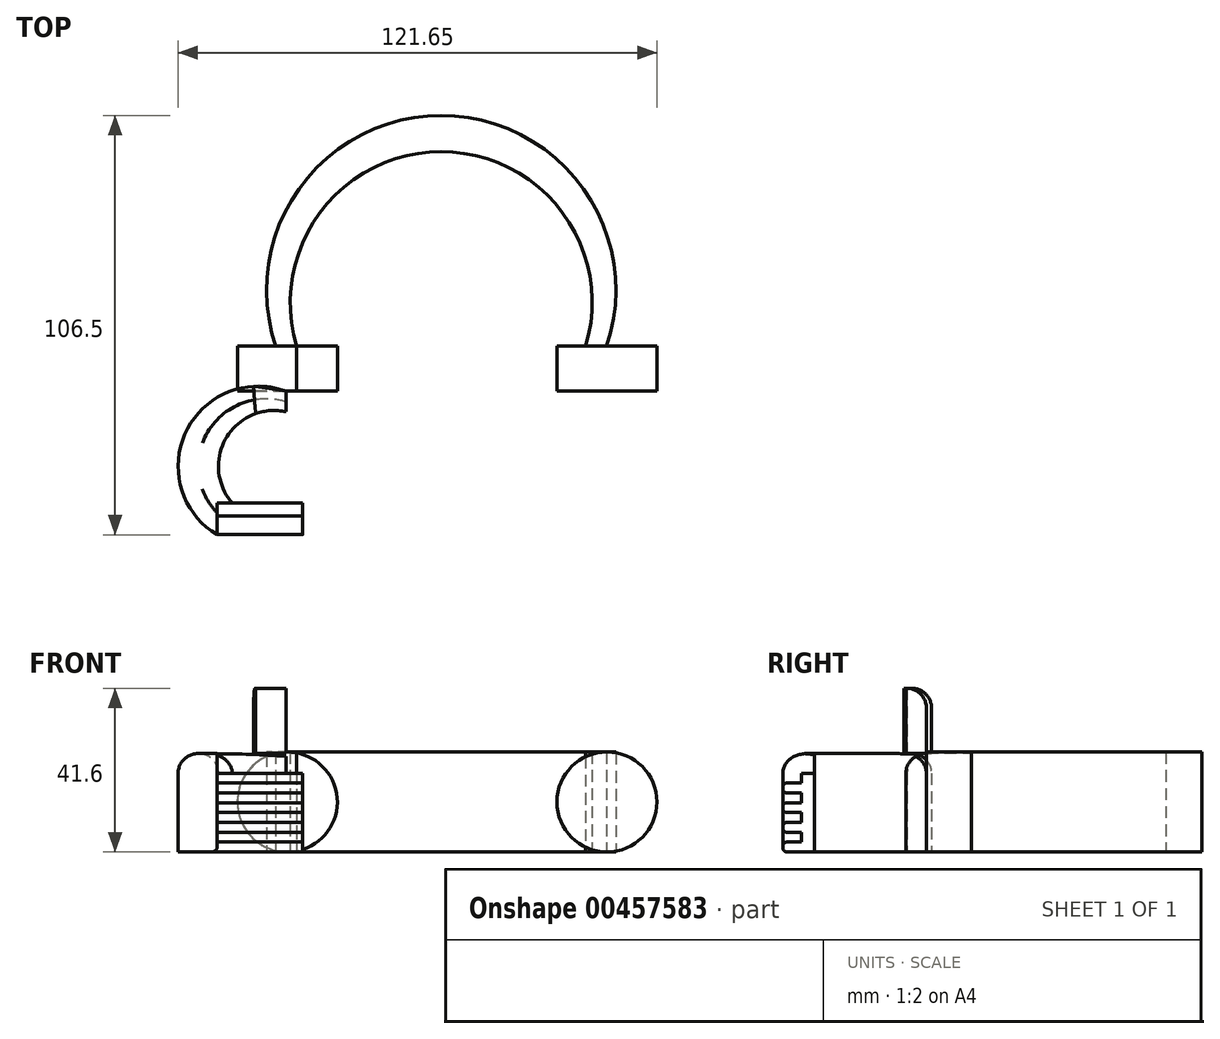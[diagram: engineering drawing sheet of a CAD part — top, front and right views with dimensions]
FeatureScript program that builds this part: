
annotation { "Feature Type Name" : "Feature", "Feature Type Description" : "" }
export const myFeature = defineFeature(function(context is Context, id is Id, definition is map)
    precondition{}
    {
        {
            var Q0;
            Q0=qCreatedBy(makeId("Top.planeOp"),FACE);
            var sketch = newSketch(context, id + "F0", { "sketchPlane" : qUnion([Q0])});
            skArc(sketch, "E0", {"start": v(46.23, 0) * mm, "mid": v(4.18, 58.57) * mm, "end": v(-37.87, 0) * mm});
            skLineSegment(sketch, "E1", {"start": v(-37.87, 0) * mm, "end": v(-32.54, 0) * mm});
            skLineSegment(sketch, "E2", {"start": v(46.23, 0) * mm, "end": v(40.9, 0) * mm});
            skArc(sketch, "E3", {"start": v(40.9, 0) * mm, "mid": v(4.18, 49.41) * mm, "end": v(-32.54, 0) * mm});
            skSolve(sketch);
        }
        {
            var Q0;
            Q0=makeQuery(id+"F0.imprint","IMPRINT",FACE,{"disambiguationData":[TD([[makeQuery(id+"F0.imprint","IMPRINT",EDGE,{"derivedFrom":sQuery(id+"F0.wireOp",EDGE,"E0")}),1.0]])]});
            extrude(context, id + "F1", {"entities" : qUnion([Q0]), "depth" : 25.4 * mm});
        }
        {
            var Q0;
            Q0=makeQuery(id+"F1.opExtrude","SWEPT_FACE",FACE,{"disambiguationData":[OSD([sQuery(id+"F0.wireOp",EDGE,"E1")])]});
            var sketch = newSketch(context, id + "F2", { "sketchPlane" : qUnion([Q0])});
            skCircle(sketch, "E4", {"center": v(-34.91, 12.7) * mm, "radius": 12.7 * mm});
            skCircle(sketch, "E5", {"center": v(46.29, 12.7) * mm, "radius": 12.7 * mm});
            skPoint(sketch, "E5.centerSnap0", {"position": v(-32.54, 12.7) * mm});
            skSolve(sketch);
        }
        {
            var Q0;
            {var subQ0=sQuery(id+"F2.wireOp",EDGE,"E4");var subQ1=makeQuery(id+"F1.opExtrude","SWEPT_EDGE",EDGE,{"disambiguationData":[OSD([sQuery(id+"F0.wireOp",EDGE,"E0"),sQuery(id+"F0.wireOp",EDGE,"E1")])]});var subQ2=makeQuery(id+"F2.imprint","INTERSECT",VERTEX,{"disambiguationData":[OD(0.0)],"derivedFrom":[subQ1,subQ0]});Q0=makeQuery(id+"F2.imprint","IMPRINT",FACE,{"disambiguationData":[TD([[makeQuery(id+"F2.imprint","IMPRINT",EDGE,{"disambiguationData":[TD([[subQ2,-1.0]])],"derivedFrom":subQ0}),1.0]])]});}
            var Q1;
            {var subQ0=sQuery(id+"F2.wireOp",EDGE,"E4");var subQ1=sQuery(id+"F0.wireOp",EDGE,"E1");var subQ5=makeQuery(id+"F2.imprint","INTERSECT",VERTEX,{"derivedFrom":[makeQuery(id+"F1.opExtrude","CAP_EDGE",EDGE,{"disambiguationData":[OSD([subQ1])],"isStart":true}),subQ0]});Q1=makeQuery(id+"F2.imprint","IMPRINT",FACE,{"disambiguationData":[TD([[makeQuery(id+"F2.imprint","IMPRINT",EDGE,{"disambiguationData":[TD([[subQ5,1.0]])],"derivedFrom":subQ0}),1.0]])]});}
            var Q2;
            {var subQ0=sQuery(id+"F2.wireOp",EDGE,"E4");var subQ1=makeQuery(id+"F1.opExtrude","SWEPT_EDGE",EDGE,{"disambiguationData":[OSD([sQuery(id+"F0.wireOp",EDGE,"E1"),sQuery(id+"F0.wireOp",EDGE,"E3")])]});var subQ2=makeQuery(id+"F2.imprint","INTERSECT",VERTEX,{"disambiguationData":[OD(0.0)],"derivedFrom":[subQ1,subQ0]});Q2=makeQuery(id+"F2.imprint","IMPRINT",FACE,{"disambiguationData":[TD([[makeQuery(id+"F2.imprint","IMPRINT",EDGE,{"disambiguationData":[TD([[subQ2,1.0]])],"derivedFrom":subQ0}),1.0]])]});}
            var Q3;
            Q3=sQuery(id+"F2.wireOp",EDGE,"E4");
            extrude(context, id + "F3", {"entities" : qUnion([Q0, Q1, Q2]), "surfaceEntities" : qUnion([Q3]), "depth" : 11.43 * mm});
        }
        {
            var Q0;
            Q0 = qSketchRegion(id + "F2", true);
            extrude(context, id + "F4", {"entities" : qUnion([Q0]), "depth" : 11.43 * mm});
        }
        {
            var Q0;
            Q0=qCreatedBy(makeId("Top.planeOp"),FACE);
            var sketch = newSketch(context, id + "F5", { "sketchPlane" : qUnion([Q0])});
            skArc(sketch, "E6", {"start": v(-35.28, -11.48) * mm, "mid": v(-62.66, -30.6) * mm, "end": v(-35.14, -49.5) * mm});
            skLineSegment(sketch, "E7", {"start": v(-35.14, -49.5) * mm, "end": v(-35.14, -44.34) * mm});
            skLineSegment(sketch, "E8", {"start": v(-35.28, -11.48) * mm, "end": v(-35.28, -16.68) * mm});
            skArc(sketch, "E9", {"start": v(-35.28, -16.68) * mm, "mid": v(-52.41, -30.6) * mm, "end": v(-35.14, -44.34) * mm});
            skSolve(sketch);
        }
        {
            var Q0;
            Q0=makeQuery(id+"F5.imprint","IMPRINT",FACE,{"disambiguationData":[TD([[makeQuery(id+"F5.imprint","IMPRINT",EDGE,{"derivedFrom":sQuery(id+"F5.wireOp",EDGE,"E6")}),1.0]])]});
            extrude(context, id + "F6", {"entities" : qUnion([Q0]), "depth" : 25 * mm});
        }
        {
            var Q0;
            Q0=qCreatedBy(makeId("Top.planeOp"),FACE);
            var sketch = newSketch(context, id + "F7", { "sketchPlane" : qUnion([Q0])});
            skLineSegment(sketch, "E10.bottom", {"start": v(-31, -39.88) * mm, "end": v(-52.8, -39.88) * mm});
            skLineSegment(sketch, "E10.top", {"start": v(-31, -55.1) * mm, "end": v(-52.8, -55.1) * mm});
            skLineSegment(sketch, "E10.left", {"start": v(-31, -39.88) * mm, "end": v(-31, -55.1) * mm});
            skLineSegment(sketch, "E10.right", {"start": v(-52.8, -39.88) * mm, "end": v(-52.8, -55.1) * mm});
            skSolve(sketch);
        }
        {
            var Q0;
            Q0 = qSketchRegion(id + "F7", true);
            extrude(context, id + "F8", {"entities" : qUnion([Q0]), "operationType" : NewBodyOperationType.ADD, "depth" : 25 * mm});
        }
        {
            var Q0;
            Q0=makeQuery(id+"F8.opExtrude","SWEPT_FACE",FACE,{"disambiguationData":[OSD([sQuery(id+"F7.wireOp",EDGE,"E10.top")])]});
            var sketch = newSketch(context, id + "F9", { "sketchPlane" : qUnion([Q0])});
            skLineSegment(sketch, "E11", {"start": v(-52.8, 2.5) * mm, "end": v(-31, 2.5) * mm});
            skLineSegment(sketch, "E12", {"start": v(-31, 2.5) * mm, "end": v(-31, 5) * mm});
            skLineSegment(sketch, "E13", {"start": v(-31, 5) * mm, "end": v(-52.8, 5) * mm});
            skLineSegment(sketch, "E14", {"start": v(-52.8, 5) * mm, "end": v(-52.8, 7.5) * mm});
            skLineSegment(sketch, "E15", {"start": v(-52.8, 7.5) * mm, "end": v(-31, 7.5) * mm});
            skLineSegment(sketch, "E16", {"start": v(-31, 7.5) * mm, "end": v(-31, 10) * mm});
            skLineSegment(sketch, "E17", {"start": v(-31, 10) * mm, "end": v(-52.8, 10) * mm});
            skLineSegment(sketch, "E18", {"start": v(-52.8, 10) * mm, "end": v(-52.8, 12.5) * mm});
            skLineSegment(sketch, "E19", {"start": v(-52.8, 12.5) * mm, "end": v(-31, 12.5) * mm});
            skLineSegment(sketch, "E20", {"start": v(-31, 12.5) * mm, "end": v(-31, 15) * mm});
            skLineSegment(sketch, "E21", {"start": v(-31, 15) * mm, "end": v(-52.8, 15) * mm});
            skLineSegment(sketch, "E22", {"start": v(-52.8, 15) * mm, "end": v(-52.8, 17.5) * mm});
            skLineSegment(sketch, "E23", {"start": v(-52.8, 17.5) * mm, "end": v(-31, 17.5) * mm});
            skLineSegment(sketch, "E24", {"start": v(-31, 17.5) * mm, "end": v(-31, 20) * mm});
            skLineSegment(sketch, "E25", {"start": v(-31, 20) * mm, "end": v(-52.8, 20) * mm});
            skLineSegment(sketch, "E26", {"start": v(-52.8, 20) * mm, "end": v(-58.32, 20) * mm});
            skLineSegment(sketch, "E27", {"start": v(-58.32, 20) * mm, "end": v(-58.32, 25) * mm});
            skLineSegment(sketch, "E28", {"start": v(-58.32, 25) * mm, "end": v(-52.8, 25) * mm});
            skSolve(sketch);
        }
        {
            var Q0;
            {var subQ0=sQuery(id+"F9.wireOp",EDGE,"E11");Q0=makeQuery(id+"F9.imprint","IMPRINT",FACE,{"disambiguationData":[TD([[makeQuery(id+"F9.imprint","IMPRINT",EDGE,{"derivedFrom":subQ0}),1.0]])]});}
            var Q1;
            {var subQ0=sQuery(id+"F9.wireOp",EDGE,"E15");Q1=makeQuery(id+"F9.imprint","IMPRINT",FACE,{"disambiguationData":[TD([[makeQuery(id+"F9.imprint","IMPRINT",EDGE,{"derivedFrom":subQ0}),1.0]])]});}
            var Q2;
            {var subQ0=sQuery(id+"F9.wireOp",EDGE,"E19");Q2=makeQuery(id+"F9.imprint","IMPRINT",FACE,{"disambiguationData":[TD([[makeQuery(id+"F9.imprint","IMPRINT",EDGE,{"derivedFrom":subQ0}),1.0]])]});}
            var Q3;
            {var subQ0=sQuery(id+"F9.wireOp",EDGE,"E23");Q3=makeQuery(id+"F9.imprint","IMPRINT",FACE,{"disambiguationData":[TD([[makeQuery(id+"F9.imprint","IMPRINT",EDGE,{"derivedFrom":subQ0}),1.0]])]});}
            extrude(context, id + "F10", {"entities" : qUnion([Q0, Q1, Q2, Q3]), "operationType" : NewBodyOperationType.REMOVE, "oppositeDirection" : true, "depth" : 11.9 * mm});
        }
        {
            var Q0;
            Q0=makeQuery(id+"F8.boolean.opBoolean","MERGE",FACE,{"derivedFrom":[makeQuery(id+"F6.opExtrude","CAP_FACE",FACE,{"disambiguationData":[OSD([sQuery(id+"F5.wireOp",EDGE,"E6"),sQuery(id+"F5.wireOp",EDGE,"E7"),sQuery(id+"F5.wireOp",EDGE,"E8"),sQuery(id+"F5.wireOp",EDGE,"E9")])],"isStart":false}),makeQuery(id+"F8.opExtrude","CAP_FACE",FACE,{"disambiguationData":[OSD([sQuery(id+"F7.wireOp",EDGE,"E10.bottom"),sQuery(id+"F7.wireOp",EDGE,"E10.top"),sQuery(id+"F7.wireOp",EDGE,"E10.left"),sQuery(id+"F7.wireOp",EDGE,"E10.right")])],"isStart":false})]});
            var sketch = newSketch(context, id + "F11", { "sketchPlane" : qUnion([Q0])});
            skLineSegment(sketch, "E29", {"start": v(-52.8, -47.93) * mm, "end": v(-31, -47.93) * mm});
            skLineSegment(sketch, "E30", {"start": v(-31, -47.93) * mm, "end": v(-31, -55.1) * mm});
            skLineSegment(sketch, "E31", {"start": v(-31, -55.1) * mm, "end": v(-52.8, -55.1) * mm});
            skLineSegment(sketch, "E32", {"start": v(-52.8, -55.1) * mm, "end": v(-52.8, -47.93) * mm});
            skSolve(sketch);
        }
        {
            var Q0;
            Q0 = qSketchRegion(id + "F11", true);
            extrude(context, id + "F12", {"entities" : qUnion([Q0]), "operationType" : NewBodyOperationType.REMOVE, "oppositeDirection" : true, "depth" : 27 * mm});
        }
        {
            var Q0;
            Q0=makeQuery(id+"F12.boolean.opBoolean","COPY",EDGE,{"derivedFrom":makeQuery(id+"F12.opExtrude","CAP_EDGE",EDGE,{"disambiguationData":[OSD([sQuery(id+"F11.wireOp",EDGE,"E29")])],"isStart":true})});
            var Q1;
            Q1=makeQuery(id+"F12.boolean.opBoolean","INTERSECT",EDGE,{"derivedFrom":[makeQuery(id+"F10.boolean.opBoolean","COPY",FACE,{"derivedFrom":makeQuery(id+"F10.opExtrude","SWEPT_FACE",FACE,{"disambiguationData":[OSD([sQuery(id+"F9.wireOp",EDGE,"E25")])]})}),makeQuery(id+"F12.opExtrude","SWEPT_FACE",FACE,{"disambiguationData":[OSD([sQuery(id+"F11.wireOp",EDGE,"E29")])]})]});
            fillet(context, id + "F13", {"entities" : qUnion([Q0, Q1]), "radius" : 2.5 * mm, "tangentPropagation" : true, "allowEdgeOverflow" : false});
        }
        {
            var Q0;
            Q0=makeQuery(id+"F12.boolean.opBoolean","INTERSECT",EDGE,{"derivedFrom":[makeQuery(id+"F10.boolean.opBoolean","COPY",FACE,{"derivedFrom":makeQuery(id+"F10.opExtrude","SWEPT_FACE",FACE,{"disambiguationData":[OSD([sQuery(id+"F9.wireOp",EDGE,"E23")])]})}),makeQuery(id+"F12.opExtrude","SWEPT_FACE",FACE,{"disambiguationData":[OSD([sQuery(id+"F11.wireOp",EDGE,"E29")])]})]});
            var Q1;
            Q1=makeQuery(id+"F12.boolean.opBoolean","INTERSECT",EDGE,{"derivedFrom":[makeQuery(id+"F10.boolean.opBoolean","COPY",FACE,{"derivedFrom":makeQuery(id+"F10.opExtrude","SWEPT_FACE",FACE,{"disambiguationData":[OSD([sQuery(id+"F9.wireOp",EDGE,"E21")])]})}),makeQuery(id+"F12.opExtrude","SWEPT_FACE",FACE,{"disambiguationData":[OSD([sQuery(id+"F11.wireOp",EDGE,"E29")])]})]});
            fillet(context, id + "F14", {"entities" : qUnion([Q0, Q1]), "radius" : 1 * mm, "tangentPropagation" : true, "allowEdgeOverflow" : false});
        }
        {
            var Q0;
            Q0=makeQuery(id+"F12.boolean.opBoolean","INTERSECT",EDGE,{"derivedFrom":[makeQuery(id+"F10.boolean.opBoolean","COPY",FACE,{"derivedFrom":makeQuery(id+"F10.opExtrude","SWEPT_FACE",FACE,{"disambiguationData":[OSD([sQuery(id+"F9.wireOp",EDGE,"E19")])]})}),makeQuery(id+"F12.opExtrude","SWEPT_FACE",FACE,{"disambiguationData":[OSD([sQuery(id+"F11.wireOp",EDGE,"E29")])]})]});
            var Q1;
            Q1=makeQuery(id+"F12.boolean.opBoolean","INTERSECT",EDGE,{"derivedFrom":[makeQuery(id+"F10.boolean.opBoolean","COPY",FACE,{"derivedFrom":makeQuery(id+"F10.opExtrude","SWEPT_FACE",FACE,{"disambiguationData":[OSD([sQuery(id+"F9.wireOp",EDGE,"E17")])]})}),makeQuery(id+"F12.opExtrude","SWEPT_FACE",FACE,{"disambiguationData":[OSD([sQuery(id+"F11.wireOp",EDGE,"E29")])]})]});
            fillet(context, id + "F15", {"entities" : qUnion([Q0, Q1]), "radius" : 1 * mm, "tangentPropagation" : true, "allowEdgeOverflow" : false});
        }
        {
            var Q0;
            Q0=makeQuery(id+"F12.boolean.opBoolean","INTERSECT",EDGE,{"derivedFrom":[makeQuery(id+"F10.boolean.opBoolean","COPY",FACE,{"derivedFrom":makeQuery(id+"F10.opExtrude","SWEPT_FACE",FACE,{"disambiguationData":[OSD([sQuery(id+"F9.wireOp",EDGE,"E15")])]})}),makeQuery(id+"F12.opExtrude","SWEPT_FACE",FACE,{"disambiguationData":[OSD([sQuery(id+"F11.wireOp",EDGE,"E29")])]})]});
            var Q1;
            Q1=makeQuery(id+"F12.boolean.opBoolean","INTERSECT",EDGE,{"derivedFrom":[makeQuery(id+"F10.boolean.opBoolean","COPY",FACE,{"derivedFrom":makeQuery(id+"F10.opExtrude","SWEPT_FACE",FACE,{"disambiguationData":[OSD([sQuery(id+"F9.wireOp",EDGE,"E13")])]})}),makeQuery(id+"F12.opExtrude","SWEPT_FACE",FACE,{"disambiguationData":[OSD([sQuery(id+"F11.wireOp",EDGE,"E29")])]})]});
            fillet(context, id + "F16", {"entities" : qUnion([Q0, Q1]), "radius" : 1 * mm, "tangentPropagation" : true, "allowEdgeOverflow" : false});
        }
        {
            var Q0;
            Q0=makeQuery(id+"F12.boolean.opBoolean","INTERSECT",EDGE,{"derivedFrom":[makeQuery(id+"F10.boolean.opBoolean","COPY",FACE,{"derivedFrom":makeQuery(id+"F10.opExtrude","SWEPT_FACE",FACE,{"disambiguationData":[OSD([sQuery(id+"F9.wireOp",EDGE,"E11")])]})}),makeQuery(id+"F12.opExtrude","SWEPT_FACE",FACE,{"disambiguationData":[OSD([sQuery(id+"F11.wireOp",EDGE,"E29")])]})]});
            var Q1;
            Q1=makeQuery(id+"F12.boolean.opBoolean","INTERSECT",EDGE,{"derivedFrom":[makeQuery(id+"F8.boolean.opBoolean","MERGE",FACE,{"derivedFrom":[makeQuery(id+"F6.opExtrude","CAP_FACE",FACE,{"disambiguationData":[OSD([sQuery(id+"F5.wireOp",EDGE,"E6"),sQuery(id+"F5.wireOp",EDGE,"E7"),sQuery(id+"F5.wireOp",EDGE,"E8"),sQuery(id+"F5.wireOp",EDGE,"E9")])],"isStart":true}),makeQuery(id+"F8.opExtrude","CAP_FACE",FACE,{"disambiguationData":[OSD([sQuery(id+"F7.wireOp",EDGE,"E10.bottom"),sQuery(id+"F7.wireOp",EDGE,"E10.top"),sQuery(id+"F7.wireOp",EDGE,"E10.left"),sQuery(id+"F7.wireOp",EDGE,"E10.right")])],"isStart":true})]}),makeQuery(id+"F12.opExtrude","SWEPT_FACE",FACE,{"disambiguationData":[OSD([sQuery(id+"F11.wireOp",EDGE,"E29")])]})]});
            fillet(context, id + "F17", {"entities" : qUnion([Q0, Q1]), "radius" : 1 * mm, "tangentPropagation" : true, "allowEdgeOverflow" : false});
        }
        {
            var Q0;
            {var subQ0=sQuery(id+"F9.wireOp",EDGE,"E25");Q0=makeQuery(id+"F9.imprint","IMPRINT",FACE,{"disambiguationData":[TD([[makeQuery(id+"F9.imprint","IMPRINT",EDGE,{"derivedFrom":subQ0}),-1.0]])]});}
            var Q1;
            Q1=makeQuery(id+"F8.opExtrude","SWEPT_FACE",FACE,{"disambiguationData":[OSD([sQuery(id+"F7.wireOp",EDGE,"E10.bottom")])]});
            extrude(context, id + "F18", {"entities" : qUnion([Q0]), "operationType" : NewBodyOperationType.REMOVE, "endBound" : BoundingType.UP_TO_SURFACE, "oppositeDirection" : true, "endBoundEntityFace" : qUnion([Q1]), "depth" : 15.4 * mm});
        }
        {
            var Q0;
            Q0=makeQuery(id+"F8.boolean.opBoolean","MERGE",FACE,{"derivedFrom":[makeQuery(id+"F6.opExtrude","CAP_FACE",FACE,{"disambiguationData":[OSD([sQuery(id+"F5.wireOp",EDGE,"E6"),sQuery(id+"F5.wireOp",EDGE,"E7"),sQuery(id+"F5.wireOp",EDGE,"E8"),sQuery(id+"F5.wireOp",EDGE,"E9")])],"isStart":false}),makeQuery(id+"F8.opExtrude","CAP_FACE",FACE,{"disambiguationData":[OSD([sQuery(id+"F7.wireOp",EDGE,"E10.bottom"),sQuery(id+"F7.wireOp",EDGE,"E10.top"),sQuery(id+"F7.wireOp",EDGE,"E10.left"),sQuery(id+"F7.wireOp",EDGE,"E10.right")])],"isStart":false})]});
            var sketch = newSketch(context, id + "F19", { "sketchPlane" : qUnion([Q0])});
            skLineSegment(sketch, "E33", {"start": v(-43.14, -10.23) * mm, "end": v(-35.28, -11.48) * mm});
            skLineSegment(sketch, "E34", {"start": v(-35.28, -11.48) * mm, "end": v(-35.28, -16.68) * mm});
            skLineSegment(sketch, "E35", {"start": v(-35.28, -16.68) * mm, "end": v(-43.02, -17.2) * mm});
            skLineSegment(sketch, "E36", {"start": v(-43.02, -17.2) * mm, "end": v(-43.5, -9.73) * mm});
            skSolve(sketch);
        }
        {
            var Q0;
            {var subQ0=sQuery(id+"F19.wireOp",EDGE,"E33");Q0=makeQuery(id+"F19.imprint","IMPRINT",FACE,{"disambiguationData":[TD([[makeQuery(id+"F19.imprint","IMPRINT",EDGE,{"derivedFrom":subQ0}),-1.0]])]});}
            extrude(context, id + "F20", {"entities" : qUnion([Q0]), "depth" : 16.6 * mm});
        }
        {
            var Q0;
            Q0=makeQuery(id+"F20.opExtrude","CAP_EDGE",EDGE,{"disambiguationData":[OSD([sQuery(id+"F19.wireOp",EDGE,"E33")])],"isStart":false});
            fillet(context, id + "F21", {"entities" : qUnion([Q0]), "radius" : 5 * mm, "tangentPropagation" : true, "allowEdgeOverflow" : false});
        }
        {
            var Q0;
            Q0=makeQuery(id+"F6.opExtrude","CAP_EDGE",EDGE,{"disambiguationData":[OSD([sQuery(id+"F5.wireOp",EDGE,"E6")])],"isStart":false});
            var Q1;
            Q1=makeQuery(id+"F6.opExtrude","CAP_EDGE",EDGE,{"disambiguationData":[OSD([sQuery(id+"F5.wireOp",EDGE,"E9")])],"isStart":false});
            fillet(context, id + "F22", {"entities" : qUnion([Q0, Q1]), "radius" : 5 * mm, "tangentPropagation" : true, "allowEdgeOverflow" : false});
        }
    });
